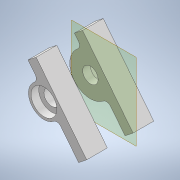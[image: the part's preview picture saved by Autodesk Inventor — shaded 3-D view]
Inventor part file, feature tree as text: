
AUTODESK INVENTOR PART (.ipt)
format: ipt  version: 2022 (Build 260153070, 153G)  size: 190,464 bytes
history: native  units: in
note: dims shown in document units (in); Inventor stores cm internally (conversion verified against a paired STEP export)
features: extrude x6, sketch x6, other x3, plane x1, reference x1
ambient origin geometry x8: Origin, YZ Plane, XZ Plane, XY Plane, X Axis, Y Axis, Z Axis, Center Point
bodies: Solid1 (feature_tree)
feature tree (17):
  extrude  "Extrusion1"  Depth=0.0787in
  extrude  "Extrusion2"  TaperAngle=90.0deg  [1 undecoded]
  plane  "Work Plane1"
  extrude  "Extrusion3"  Depth=0.1969in
  extrude  "Extrusion4"  Depth=0.1969in
  extrude  "Extrusion5"  Depth=0.2165in
  extrude  "Extrusion6"  Depth=0.1575in
  sketch  "Sketch2"  dims[d0=0.0591in d1=0.0787in]
  reference  "Reference1"
  sketch  "Sketch3"  dims[d3=90.0deg d4=90.0deg]
  sketch  "Sketch4"  dims[d5=0.1575in d6=0.0in d7=0.1969in]
  sketch  "Sketch5"  dims[d8=0.0591in d9=0.0in d10=0.1969in]
  sketch  "Sketch6"  dims[d11=0.1575in d12=0.0in d13=0.2165in]
  sketch  "Sketch7"  dims[d15=0.0984in d16=0.0in d17=0.1575in d18=0.0787in d19=0.0in d20=0.5787in d21=0.0in]
  other  "<userpath> laptop\Desktop\Custom3dpFanDuct\REF_MODEL\ENDER 3 ASSEMBLY.iam"
  other  "ENDER 3 ASSEMBLY.iam"
  other  "FRONTPLATE:1"
note: 1 required parameter value undecoded (feature->parameter linkage not recoverable at this tier; creation-order binding heuristic only, values carry confidence <= 0.55)
